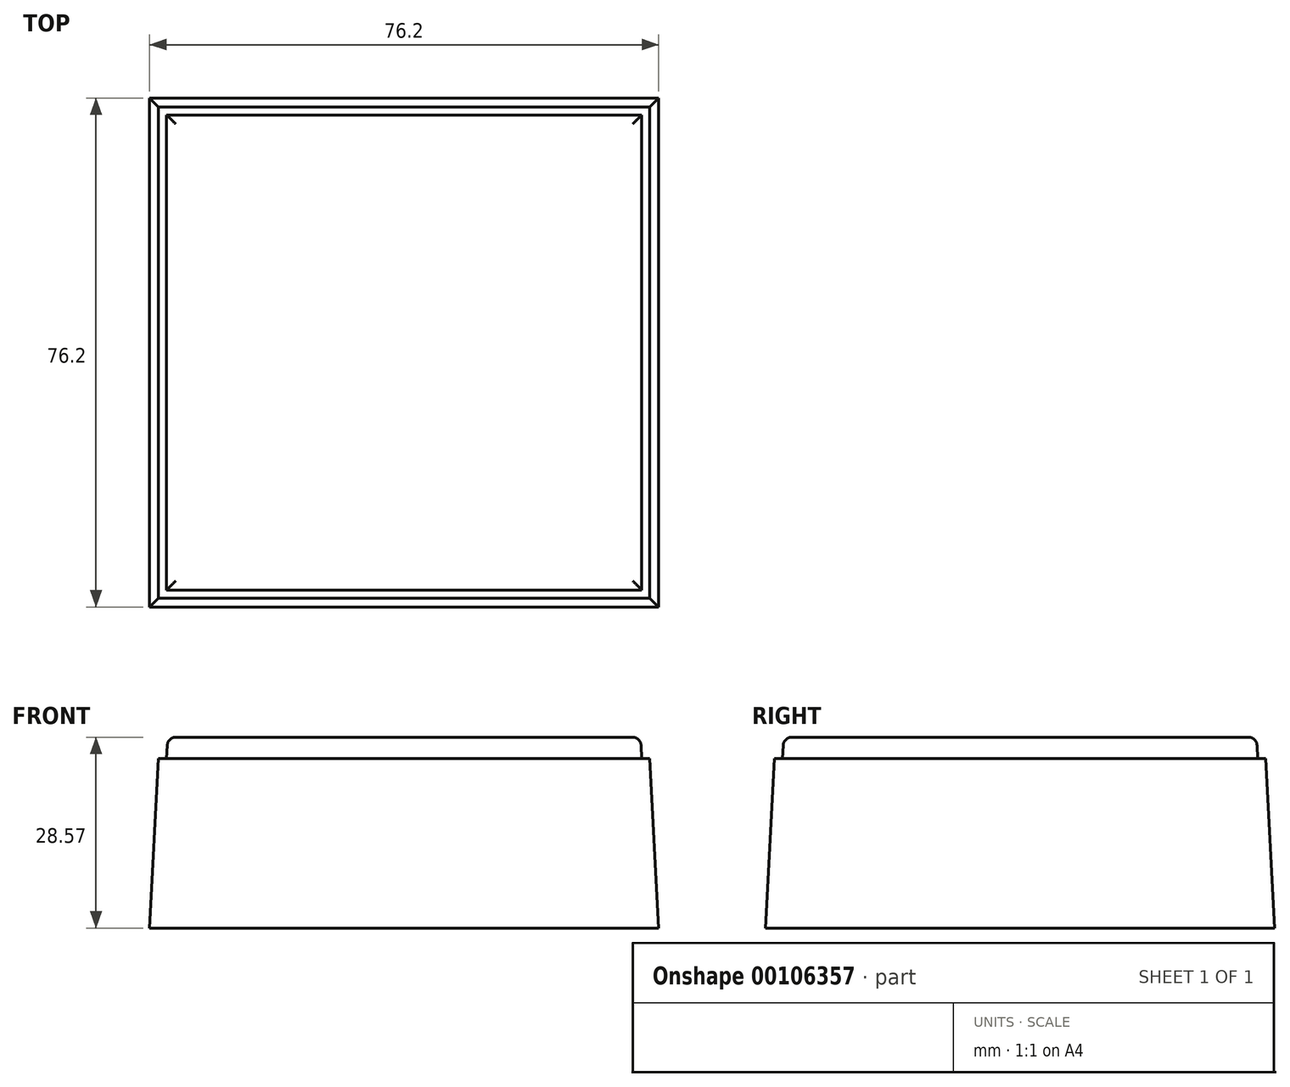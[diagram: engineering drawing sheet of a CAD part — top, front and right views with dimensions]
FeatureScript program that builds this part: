
annotation { "Feature Type Name" : "Feature", "Feature Type Description" : "" }
export const myFeature = defineFeature(function(context is Context, id is Id, definition is map)
    precondition{}
    {
        {
            var Q0;
            Q0=qCreatedBy(makeId("Top.planeOp"),FACE);
            var sketch = newSketch(context, id + "F0", { "sketchPlane" : qUnion([Q0])});
            skLineSegment(sketch, "E0.bottom", {"start": v(-38.1, 38.1) * mm, "end": v(38.1, 38.1) * mm});
            skLineSegment(sketch, "E0.top", {"start": v(-38.1, -38.1) * mm, "end": v(38.1, -38.1) * mm});
            skLineSegment(sketch, "E0.left", {"start": v(-38.1, 38.1) * mm, "end": v(-38.1, -38.1) * mm});
            skLineSegment(sketch, "E0.right", {"start": v(38.1, 38.1) * mm, "end": v(38.1, -38.1) * mm});
            skLineSegment(sketch, "E1", {"start": v(0, 38.1) * mm, "end": v(0, -38.1) * mm});
            skLineSegment(sketch, "E2", {"start": v(38.1, 0) * mm, "end": v(-38.1, 0) * mm});
            skSolve(sketch);
        }
        {
            var Q0;
            Q0 = qSketchRegion(id + "F0", true);
            extrude(context, id + "F1", {"entities" : qUnion([Q0]), "depth" : 25.4 * mm, "hasDraft" : true, "draftAngle" : 3 * degree, "draftPullDirection" : true});
        }
        {
            var Q0;
            Q0=makeQuery(id+"F1.opExtrude","CAP_FACE",FACE,{"disambiguationData":[OSD([sQuery(id+"F0.wireOp",EDGE,"E0.bottom"),sQuery(id+"F0.wireOp",EDGE,"E0.top"),sQuery(id+"F0.wireOp",EDGE,"E0.left"),sQuery(id+"F0.wireOp",EDGE,"E0.right")])],"isStart":false});
            var sketch = newSketch(context, id + "F2", { "sketchPlane" : qUnion([Q0])});
            skLineSegment(sketch, "E3.bottom", {"start": v(35.56, -35.56) * mm, "end": v(-35.56, -35.56) * mm});
            skLineSegment(sketch, "E3.top", {"start": v(35.56, 35.56) * mm, "end": v(-35.56, 35.56) * mm});
            skLineSegment(sketch, "E3.left", {"start": v(35.56, -35.56) * mm, "end": v(35.56, 35.56) * mm});
            skLineSegment(sketch, "E3.right", {"start": v(-35.56, -35.56) * mm, "end": v(-35.56, 35.56) * mm});
            skPoint(sketch, "E3.middle", {"position": v(0, 0) * mm});
            skSolve(sketch);
        }
        {
            var Q0;
            Q0 = qSketchRegion(id + "F2", true);
            extrude(context, id + "F3", {"entities" : qUnion([Q0]), "operationType" : NewBodyOperationType.ADD, "depth" : 3.17 * mm, "hasDraft" : true, "draftAngle" : 3 * degree, "draftPullDirection" : true});
        }
        {
            var Q0;
            Q0=makeQuery(id+"F3.opExtrude","CAP_EDGE",EDGE,{"disambiguationData":[OSD([sQuery(id+"F2.wireOp",EDGE,"E3.bottom")])],"isStart":false});
            var Q1;
            Q1=makeQuery(id+"F3.opExtrude","CAP_EDGE",EDGE,{"disambiguationData":[OSD([sQuery(id+"F2.wireOp",EDGE,"E3.left")])],"isStart":false});
            var Q2;
            Q2=makeQuery(id+"F3.opExtrude","CAP_EDGE",EDGE,{"disambiguationData":[OSD([sQuery(id+"F2.wireOp",EDGE,"E3.right")])],"isStart":false});
            var Q3;
            Q3=makeQuery(id+"F3.opExtrude","CAP_EDGE",EDGE,{"disambiguationData":[OSD([sQuery(id+"F2.wireOp",EDGE,"E3.top")])],"isStart":false});
            var Q4;
            Q4=makeQuery(id+"F3.opExtrude","CAP_EDGE",EDGE,{"disambiguationData":[OSD([sQuery(id+"F2.wireOp",EDGE,"E3.top")])],"isStart":true});
            var Q5;
            Q5=makeQuery(id+"F3.opExtrude","CAP_EDGE",EDGE,{"disambiguationData":[OSD([sQuery(id+"F2.wireOp",EDGE,"E3.right")])],"isStart":true});
            var Q6;
            Q6=makeQuery(id+"F3.opExtrude","CAP_EDGE",EDGE,{"disambiguationData":[OSD([sQuery(id+"F2.wireOp",EDGE,"E3.bottom")])],"isStart":true});
            var Q7;
            Q7=makeQuery(id+"F5.opExtrude","CAP_EDGE",EDGE,{"disambiguationData":[OSD([sQuery(id+"FqUhn75MxsZ1mFn_1.wireOp",EDGE,"qvLmAjp1-HQqF-UUDb-9stR-KdAxYaR9wxGp.left")])],"isStart":true});
            fillet(context, id + "F6", {"entities" : qUnion([Q0, Q1, Q2, Q3, Q4, Q5, Q6, Q7]), "radius" : 1.27 * mm, "tangentPropagation" : true, "allowEdgeOverflow" : false});
        }
    });
